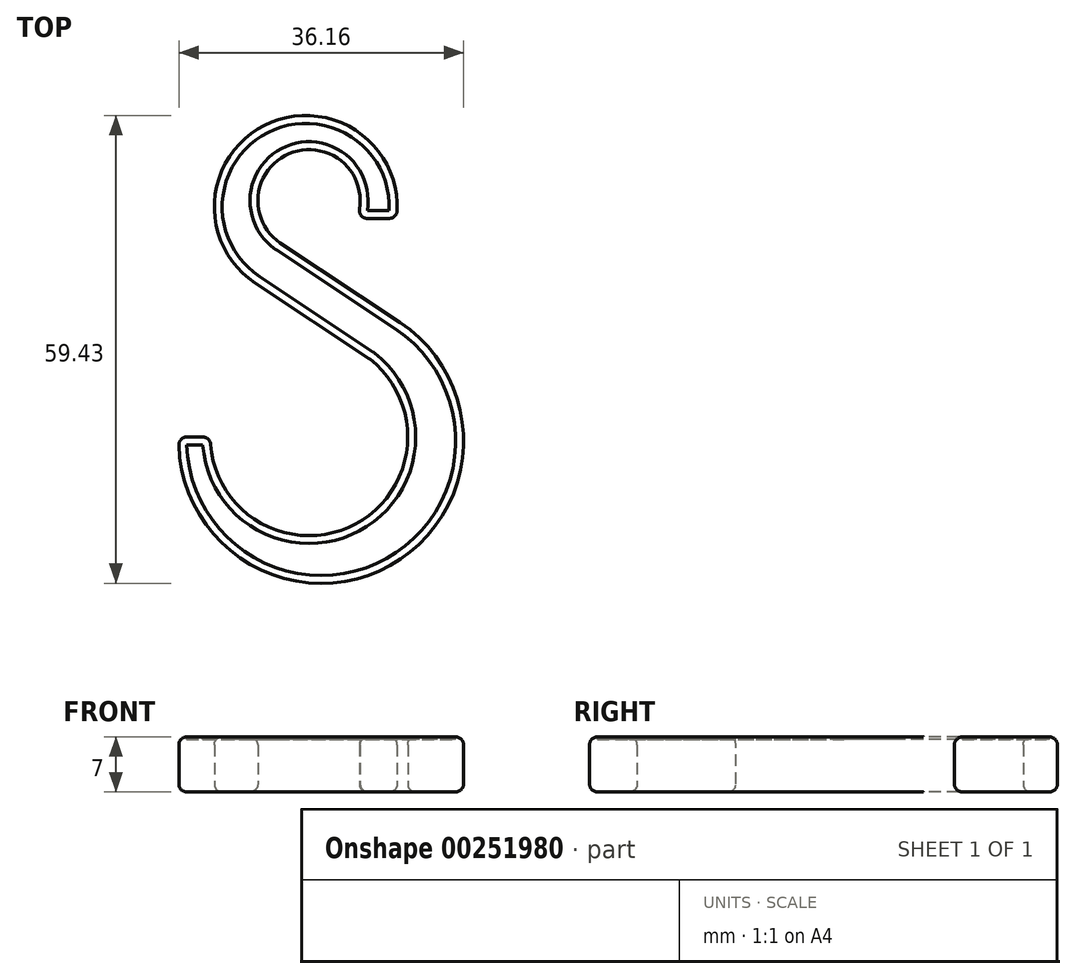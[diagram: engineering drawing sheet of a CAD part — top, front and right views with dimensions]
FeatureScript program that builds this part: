
annotation { "Feature Type Name" : "Feature", "Feature Type Description" : "" }
export const myFeature = defineFeature(function(context is Context, id is Id, definition is map)
    precondition{}
    {
        {
            var Q0;
            Q0=qCreatedBy(makeId("Top.planeOp"),FACE);
            var sketch = newSketch(context, id + "F0", { "sketchPlane" : qUnion([Q0])});
            skArc(sketch, "E0", {"start": v(6.1, -2.25) * mm, "mid": v(-1.97, 6.2) * mm, "end": v(-3.68, -5.36) * mm});
            skArc(sketch, "E1", {"start": v(-12.54, -30) * mm, "mid": v(5.51, -41.26) * mm, "end": v(7.7, -20.1) * mm});
            skArc(sketch, "E2.0", {"start": v(11.1, -2.25) * mm, "mid": v(-5.26, 9.78) * mm, "end": v(-6.84, -10.46) * mm});
            skArc(sketch, "E3.0", {"start": v(-16.54, -30) * mm, "mid": v(9.86, -46.56) * mm, "end": v(11.53, -15.45) * mm});
            skLineSegment(sketch, "E4", {"start": v(-3.68, -5.36) * mm, "end": v(11.53, -15.45) * mm});
            skLineSegment(sketch, "E5", {"start": v(-6.84, -10.46) * mm, "end": v(7.7, -20.1) * mm});
            skLineSegment(sketch, "E6", {"start": v(-16.54, -30) * mm, "end": v(-12.54, -30) * mm});
            skLineSegment(sketch, "E7", {"start": v(11.1, -2.25) * mm, "end": v(6.1, -2.25) * mm});
            skSolve(sketch);
        }
        {
            var Q0;
            Q0=makeQuery(id+"F0.imprint","IMPRINT",FACE,{"disambiguationData":[TD([[makeQuery(id+"F0.imprint","IMPRINT",EDGE,{"derivedFrom":sQuery(id+"F0.wireOp",EDGE,"E0")}),-1.0]])]});
            extrude(context, id + "F1", {"entities" : qUnion([Q0]), "depth" : 7 * mm});
        }
        {
            var Q0;
            Q0=makeQuery(id+"F1.opExtrude","SWEPT_FACE",FACE,{"disambiguationData":[OSD([sQuery(id+"F0.wireOp",EDGE,"E0")])]});
            var Q1;
            Q1=makeQuery(id+"F1.opExtrude","CAP_FACE",FACE,{"disambiguationData":[OSD([sQuery(id+"F0.wireOp",EDGE,"E0"),sQuery(id+"F0.wireOp",EDGE,"E1"),sQuery(id+"F0.wireOp",EDGE,"E2.0"),sQuery(id+"F0.wireOp",EDGE,"E3.0"),sQuery(id+"F0.wireOp",EDGE,"E4"),sQuery(id+"F0.wireOp",EDGE,"E5"),sQuery(id+"F0.wireOp",EDGE,"E6"),sQuery(id+"F0.wireOp",EDGE,"E7")])],"isStart":true});
            var Q2;
            Q2=makeQuery(id+"F1.opExtrude","CAP_FACE",FACE,{"disambiguationData":[OSD([sQuery(id+"F0.wireOp",EDGE,"E0"),sQuery(id+"F0.wireOp",EDGE,"E1"),sQuery(id+"F0.wireOp",EDGE,"E2.0"),sQuery(id+"F0.wireOp",EDGE,"E3.0"),sQuery(id+"F0.wireOp",EDGE,"E4"),sQuery(id+"F0.wireOp",EDGE,"E5"),sQuery(id+"F0.wireOp",EDGE,"E6"),sQuery(id+"F0.wireOp",EDGE,"E7")])],"isStart":false});
            var Q3;
            Q3=makeQuery(id+"F1.opExtrude","SWEPT_FACE",FACE,{"disambiguationData":[OSD([sQuery(id+"F0.wireOp",EDGE,"E1")])]});
            var Q4;
            Q4=makeQuery(id+"F1.opExtrude","SWEPT_FACE",FACE,{"disambiguationData":[OSD([sQuery(id+"F0.wireOp",EDGE,"E2.0")])]});
            var Q5;
            Q5=makeQuery(id+"F1.opExtrude","SWEPT_FACE",FACE,{"disambiguationData":[OSD([sQuery(id+"F0.wireOp",EDGE,"E3.0")])]});
            var Q6;
            Q6=makeQuery(id+"F1.opExtrude","SWEPT_FACE",FACE,{"disambiguationData":[OSD([sQuery(id+"F0.wireOp",EDGE,"E4")])]});
            var Q7;
            Q7=makeQuery(id+"F1.opExtrude","SWEPT_FACE",FACE,{"disambiguationData":[OSD([sQuery(id+"F0.wireOp",EDGE,"E5")])]});
            var Q8;
            Q8=makeQuery(id+"F1.opExtrude","SWEPT_FACE",FACE,{"disambiguationData":[OSD([sQuery(id+"F0.wireOp",EDGE,"E6")])]});
            var Q9;
            Q9=makeQuery(id+"F1.opExtrude","SWEPT_FACE",FACE,{"disambiguationData":[OSD([sQuery(id+"F0.wireOp",EDGE,"E7")])]});
            fillet(context, id + "F2", {"entities" : qUnion([Q0, Q1, Q2, Q3, Q4, Q5, Q6, Q7, Q8, Q9]), "radius" : 1 * mm, "tangentPropagation" : true, "allowEdgeOverflow" : false});
        }
        {
            var Q0;
            Q0=makeQuery(id+"F1.opExtrude","CAP_FACE",FACE,{"disambiguationData":[OSD([sQuery(id+"F0.wireOp",EDGE,"E0"),sQuery(id+"F0.wireOp",EDGE,"E1"),sQuery(id+"F0.wireOp",EDGE,"E2.0"),sQuery(id+"F0.wireOp",EDGE,"E3.0"),sQuery(id+"F0.wireOp",EDGE,"E4"),sQuery(id+"F0.wireOp",EDGE,"E5"),sQuery(id+"F0.wireOp",EDGE,"E6"),sQuery(id+"F0.wireOp",EDGE,"E7")])],"isStart":false});
            extrude(context, id + "F3", {"entities" : qUnion([Q0]), "operationType" : NewBodyOperationType.REMOVE, "oppositeDirection" : true, "depth" : 0.3 * mm});
        }
    });
